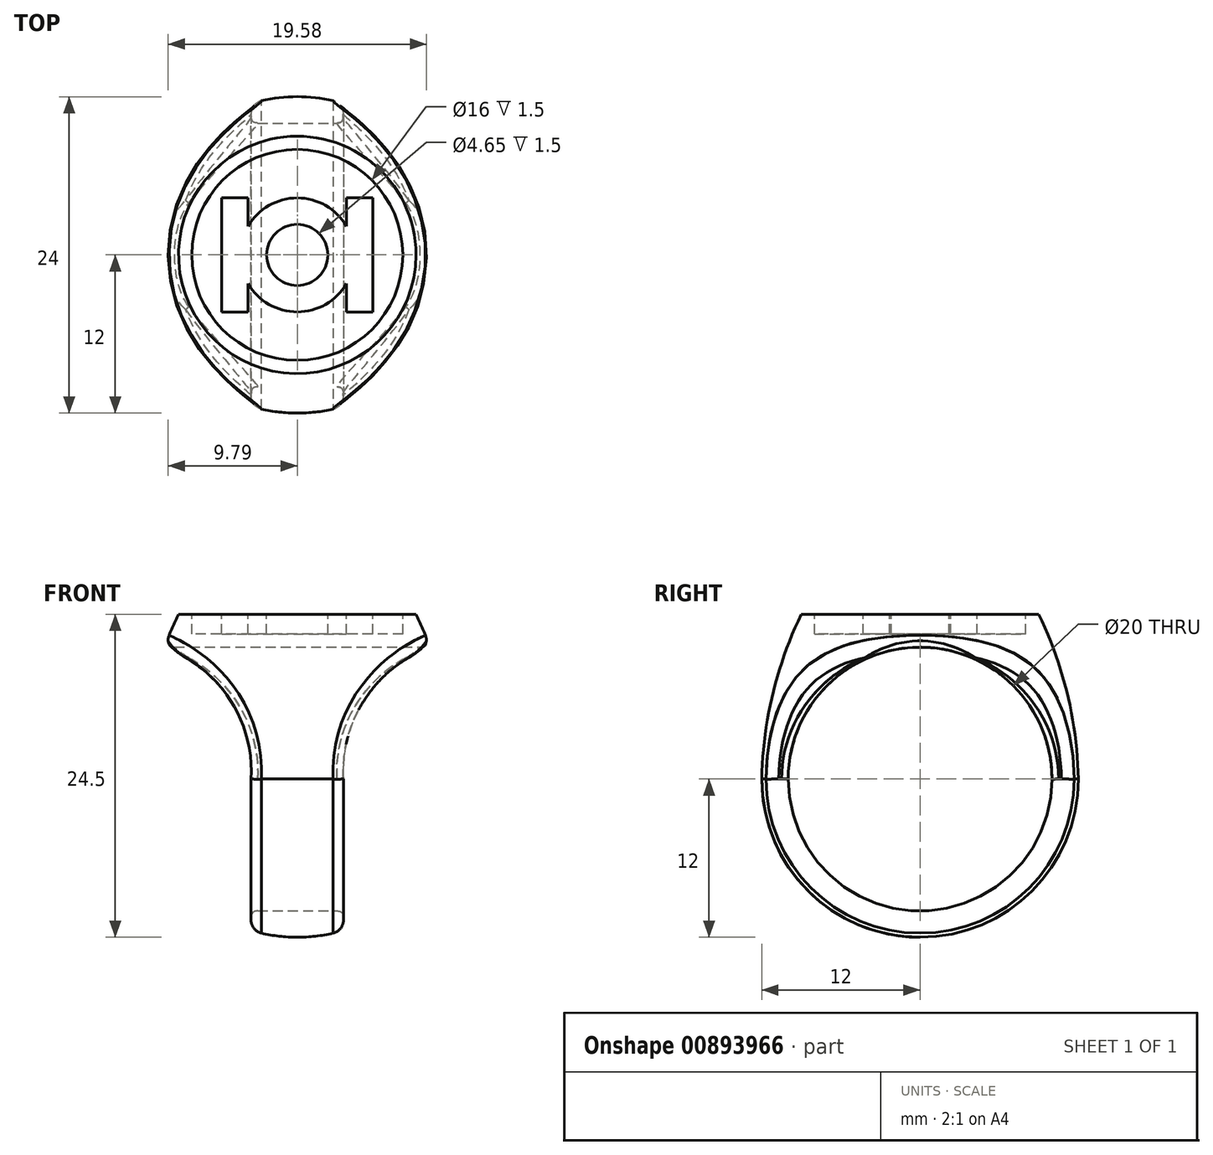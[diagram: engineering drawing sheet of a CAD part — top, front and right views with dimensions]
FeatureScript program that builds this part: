
annotation { "Feature Type Name" : "Feature", "Feature Type Description" : "" }
export const myFeature = defineFeature(function(context is Context, id is Id, definition is map)
    precondition{}
    {
        {
            var Q0;
            Q0=qCreatedBy(makeId("Right.planeOp"),FACE);
            var sketch = newSketch(context, id + "F0", { "sketchPlane" : qUnion([Q0])});
            skLineSegment(sketch, "E0", {"start": v(0, 0) * mm, "end": v(0, -24.5) * mm});
            skLineSegment(sketch, "E1", {"start": v(0, 0) * mm, "end": v(-9, 0) * mm});
            skArc(sketch, "E2", {"start": v(-12, -12.5) * mm, "mid": v(-8.49, -20.99) * mm, "end": v(0, -24.5) * mm});
            skLineSegment(sketch, "E3", {"start": v(0, -12.5) * mm, "end": v(-12, -12.5) * mm, "construction": true});
            skArc(sketch, "E4", {"start": v(-9, 0) * mm, "mid": v(-11.18, -6.09) * mm, "end": v(-12, -12.5) * mm});
            skSolve(sketch);
        }
        {
            var Q0;
            Q0=makeQuery(id+"F0.imprint","IMPRINT",FACE,{"disambiguationData":[TD([[makeQuery(id+"F0.imprint","IMPRINT",EDGE,{"derivedFrom":sQuery(id+"F0.wireOp",EDGE,"E0")}),-1.0]])]});
            var Q1;
            Q1=sQuery(id+"F0.wireOp",EDGE,"E0");
            revolve(context, id + "F1", {"entities" : qUnion([Q0]), "axis" : qUnion([Q1]), "revolveType" : RevolveType.FULL});
        }
        {
            var Q0;
            Q0=qCreatedBy(makeId("Right.planeOp"),FACE);
            var sketch = newSketch(context, id + "F2", { "sketchPlane" : qUnion([Q0])});
            skCircle(sketch, "E5", {"center": v(0, -12.5) * mm, "radius": 10 * mm});
            skSolve(sketch);
        }
        {
            var Q0;
            Q0=qSketchRegion(id+"F2",true);
            extrude(context, id + "F3", {"entities" : qUnion([Q0]), "operationType" : NewBodyOperationType.REMOVE, "oppositeDirection" : true, "depth" : 25 * mm, "offsetDistance" : 25 * mm, "symmetric" : true});
        }
        {
            var Q0;
            Q0=qCreatedBy(makeId("Front.planeOp"),FACE);
            var sketch = newSketch(context, id + "F4", { "sketchPlane" : qUnion([Q0])});
            skLineSegment(sketch, "E6", {"start": v(3.5, -26.5) * mm, "end": v(3.5, -12.5) * mm});
            skArc(sketch, "E7", {"start": v(10.15, -2.5) * mm, "mid": v(5.16, -6.39) * mm, "end": v(3.5, -12.5) * mm});
            skLineSegment(sketch, "E8", {"start": v(10.15, -2.5) * mm, "end": v(11.65, -2.5) * mm});
            skLineSegment(sketch, "E9", {"start": v(11.65, -2.5) * mm, "end": v(11.65, -26.5) * mm});
            skLineSegment(sketch, "E10", {"start": v(11.65, -26.5) * mm, "end": v(3.5, -26.5) * mm});
            skPoint(sketch, "E11.start.orphan", {"position": v(0, -24.5) * mm});
            skLineSegment(sketch, "E12", {"start": v(0, 0) * mm, "end": v(0, -24.5) * mm, "construction": true});
            skLineSegment(sketch, "E13.MirrorCS", {"start": v(-3.5, -26.5) * mm, "end": v(-3.5, -12.5) * mm});
            skArc(sketch, "E14.MirrorCS", {"start": v(-10.15, -2.5) * mm, "mid": v(-5.16, -6.39) * mm, "end": v(-3.5, -12.5) * mm});
            skLineSegment(sketch, "E15.MirrorCS", {"start": v(-11.65, -2.5) * mm, "end": v(-11.65, -26.5) * mm});
            skLineSegment(sketch, "E16.MirrorCS", {"start": v(-11.65, -26.5) * mm, "end": v(-3.5, -26.5) * mm});
            skLineSegment(sketch, "E17.MirrorCS", {"start": v(-10.15, -2.5) * mm, "end": v(-11.65, -2.5) * mm});
            skSolve(sketch);
        }
        {
            var Q0;
            Q0=qSketchRegion(id+"F4",true);
            extrude(context, id + "F5", {"entities" : qUnion([Q0]), "operationType" : NewBodyOperationType.REMOVE, "depth" : 25 * mm, "offsetDistance" : 25 * mm, "symmetric" : true});
        }
        {
            var Q0;
            Q0=makeQuery(id+"F1.opRevolve","SWEPT_FACE",FACE,{"disambiguationData":[OSD([sQuery(id+"F0.wireOp",EDGE,"E1")])]});
            var sketch = newSketch(context, id + "F6", { "sketchPlane" : qUnion([Q0])});
            skCircle(sketch, "E18", {"center": v(0, 0) * mm, "radius": 8 * mm});
            skLineSegment(sketch, "E19", {"start": v(-8, 0) * mm, "end": v(8, 0) * mm, "construction": true});
            skArc(sketch, "E20", {"start": v(-3.73, -2.18) * mm, "mid": v(0, -4.32) * mm, "end": v(3.73, -2.18) * mm});
            skLineSegment(sketch, "E21", {"start": v(-6.73, -4.32) * mm, "end": v(6.73, -4.32) * mm, "construction": true});
            skLineSegment(sketch, "E22", {"start": v(-6.73, 4.32) * mm, "end": v(6.73, 4.32) * mm, "construction": true});
            skCircle(sketch, "E23", {"center": v(0, 0) * mm, "radius": 2.32 * mm});
            skLineSegment(sketch, "E24.bottom", {"start": v(5.73, 4.32) * mm, "end": v(3.73, 4.32) * mm});
            skLineSegment(sketch, "E24.top", {"start": v(5.73, -4.32) * mm, "end": v(3.73, -4.32) * mm});
            skLineSegment(sketch, "E24.left", {"start": v(5.73, 4.32) * mm, "end": v(5.73, -4.32) * mm});
            skLineSegment(sketch, "E24.right", {"start": v(3.73, 4.32) * mm, "end": v(3.73, 2.18) * mm});
            skLineSegment(sketch, "E25.bottom", {"start": v(-5.73, 4.32) * mm, "end": v(-3.73, 4.32) * mm});
            skLineSegment(sketch, "E25.top", {"start": v(-5.73, -4.32) * mm, "end": v(-3.73, -4.32) * mm});
            skLineSegment(sketch, "E25.left", {"start": v(-5.73, 4.32) * mm, "end": v(-5.73, -4.32) * mm});
            skLineSegment(sketch, "E25.right", {"start": v(-3.73, 4.32) * mm, "end": v(-3.73, 2.18) * mm});
            skLineSegment(sketch, "E26.trimOffspring", {"start": v(-3.73, 0) * mm, "end": v(-3.73, -4.32) * mm});
            skArc(sketch, "E27.trimOffspring", {"start": v(3.73, 2.18) * mm, "mid": v(0, 4.32) * mm, "end": v(-3.73, 2.18) * mm});
            skLineSegment(sketch, "E28.trimOffspring", {"start": v(3.73, -2.18) * mm, "end": v(3.73, -4.32) * mm});
            skSolve(sketch);
        }
        {
            var Q0;
            Q0=qSketchRegion(id+"F6",true);
            var Q1;
            Q1=makeQuery(id+"F6.imprint","IMPRINT",FACE,{"disambiguationData":[TD([[makeQuery(id+"F6.imprint","IMPRINT",EDGE,{"derivedFrom":sQuery(id+"F6.wireOp",EDGE,"E23")}),1.0]])]});
            extrude(context, id + "F7", {"entities" : qUnion([Q0, Q1]), "operationType" : NewBodyOperationType.REMOVE, "oppositeDirection" : true, "depth" : 1.5 * mm, "offsetDistance" : 25 * mm});
        }
        {
            var Q0;
            Q0=makeQuery(id+"F5.boolean.opBoolean","INTERSECT",EDGE,{"disambiguationData":[OD(1.0)],"derivedFrom":[makeQuery(id+"F1.opRevolve","SWEPT_FACE",FACE,{"disambiguationData":[OSD([sQuery(id+"F0.wireOp",EDGE,"E4")])]}),makeQuery(id+"F5.opExtrude","SWEPT_FACE",FACE,{"disambiguationData":[OSD([sQuery(id+"F4.wireOp",EDGE,"E14.MirrorCS")])]})]});
            var Q1;
            Q1=makeQuery(id+"F5.boolean.opBoolean","INTERSECT",EDGE,{"derivedFrom":[makeQuery(id+"F1.opRevolve","SWEPT_FACE",FACE,{"disambiguationData":[OSD([sQuery(id+"F0.wireOp",EDGE,"E2")])]}),makeQuery(id+"F5.opExtrude","SWEPT_FACE",FACE,{"disambiguationData":[OSD([sQuery(id+"F4.wireOp",EDGE,"E13.MirrorCS")])]})]});
            var Q2;
            Q2=makeQuery(id+"F5.boolean.opBoolean","INTERSECT",EDGE,{"disambiguationData":[OD(1.0)],"derivedFrom":[makeQuery(id+"F1.opRevolve","SWEPT_FACE",FACE,{"disambiguationData":[OSD([sQuery(id+"F0.wireOp",EDGE,"E4")])]}),makeQuery(id+"F5.opExtrude","SWEPT_FACE",FACE,{"disambiguationData":[OSD([sQuery(id+"F4.wireOp",EDGE,"E7")])]})]});
            var Q3;
            Q3=makeQuery(id+"F5.boolean.opBoolean","INTERSECT",EDGE,{"derivedFrom":[makeQuery(id+"F1.opRevolve","SWEPT_FACE",FACE,{"disambiguationData":[OSD([sQuery(id+"F0.wireOp",EDGE,"E2")])]}),makeQuery(id+"F5.opExtrude","SWEPT_FACE",FACE,{"disambiguationData":[OSD([sQuery(id+"F4.wireOp",EDGE,"E6")])]})]});
            fillet(context, id + "F8", {"entities" : qUnion([Q0, Q1, Q2, Q3]), "radius" : 1 * mm, "allowEdgeOverflow" : false});
        }
        {
            var Q0;
            Q0=makeQuery(id+"F5.boolean.opBoolean","INTERSECT",EDGE,{"disambiguationData":[OD(1.0)],"derivedFrom":[makeQuery(id+"F3.boolean.opBoolean","COPY",FACE,{"derivedFrom":makeQuery(id+"F3.opExtrude","SWEPT_FACE",FACE,{"disambiguationData":[OSD([sQuery(id+"F2.wireOp",EDGE,"E5")])]})}),makeQuery(id+"F5.opExtrude","SWEPT_FACE",FACE,{"disambiguationData":[OSD([sQuery(id+"F4.wireOp",EDGE,"E14.MirrorCS")])]})]});
            var Q1;
            Q1=makeQuery(id+"F5.boolean.opBoolean","INTERSECT",EDGE,{"derivedFrom":[makeQuery(id+"F3.boolean.opBoolean","COPY",FACE,{"derivedFrom":makeQuery(id+"F3.opExtrude","SWEPT_FACE",FACE,{"disambiguationData":[OSD([sQuery(id+"F2.wireOp",EDGE,"E5")])]})}),makeQuery(id+"F5.opExtrude","SWEPT_FACE",FACE,{"disambiguationData":[OSD([sQuery(id+"F4.wireOp",EDGE,"E13.MirrorCS")])]})]});
            var Q2;
            Q2=makeQuery(id+"F5.boolean.opBoolean","INTERSECT",EDGE,{"disambiguationData":[OD(0.0)],"derivedFrom":[makeQuery(id+"F3.boolean.opBoolean","COPY",FACE,{"derivedFrom":makeQuery(id+"F3.opExtrude","SWEPT_FACE",FACE,{"disambiguationData":[OSD([sQuery(id+"F2.wireOp",EDGE,"E5")])]})}),makeQuery(id+"F5.opExtrude","SWEPT_FACE",FACE,{"disambiguationData":[OSD([sQuery(id+"F4.wireOp",EDGE,"E14.MirrorCS")])]})]});
            var Q3;
            Q3=makeQuery(id+"F5.boolean.opBoolean","INTERSECT",EDGE,{"disambiguationData":[OD(0.0)],"derivedFrom":[makeQuery(id+"F3.boolean.opBoolean","COPY",FACE,{"derivedFrom":makeQuery(id+"F3.opExtrude","SWEPT_FACE",FACE,{"disambiguationData":[OSD([sQuery(id+"F2.wireOp",EDGE,"E5")])]})}),makeQuery(id+"F5.opExtrude","SWEPT_FACE",FACE,{"disambiguationData":[OSD([sQuery(id+"F4.wireOp",EDGE,"E7")])]})]});
            var Q4;
            Q4=makeQuery(id+"F3.boolean.opBoolean","COPY",FACE,{"derivedFrom":makeQuery(id+"F3.opExtrude","SWEPT_FACE",FACE,{"disambiguationData":[OSD([sQuery(id+"F2.wireOp",EDGE,"E5")])]})});
            fillet(context, id + "F9", {"entities" : qUnion([Q0, Q1, Q2, Q3, Q4]), "radius" : .5 * mm, "rho" : 0.5, "crossSection" : FilletCrossSection.CONIC, "allowEdgeOverflow" : false});
        }
    });
